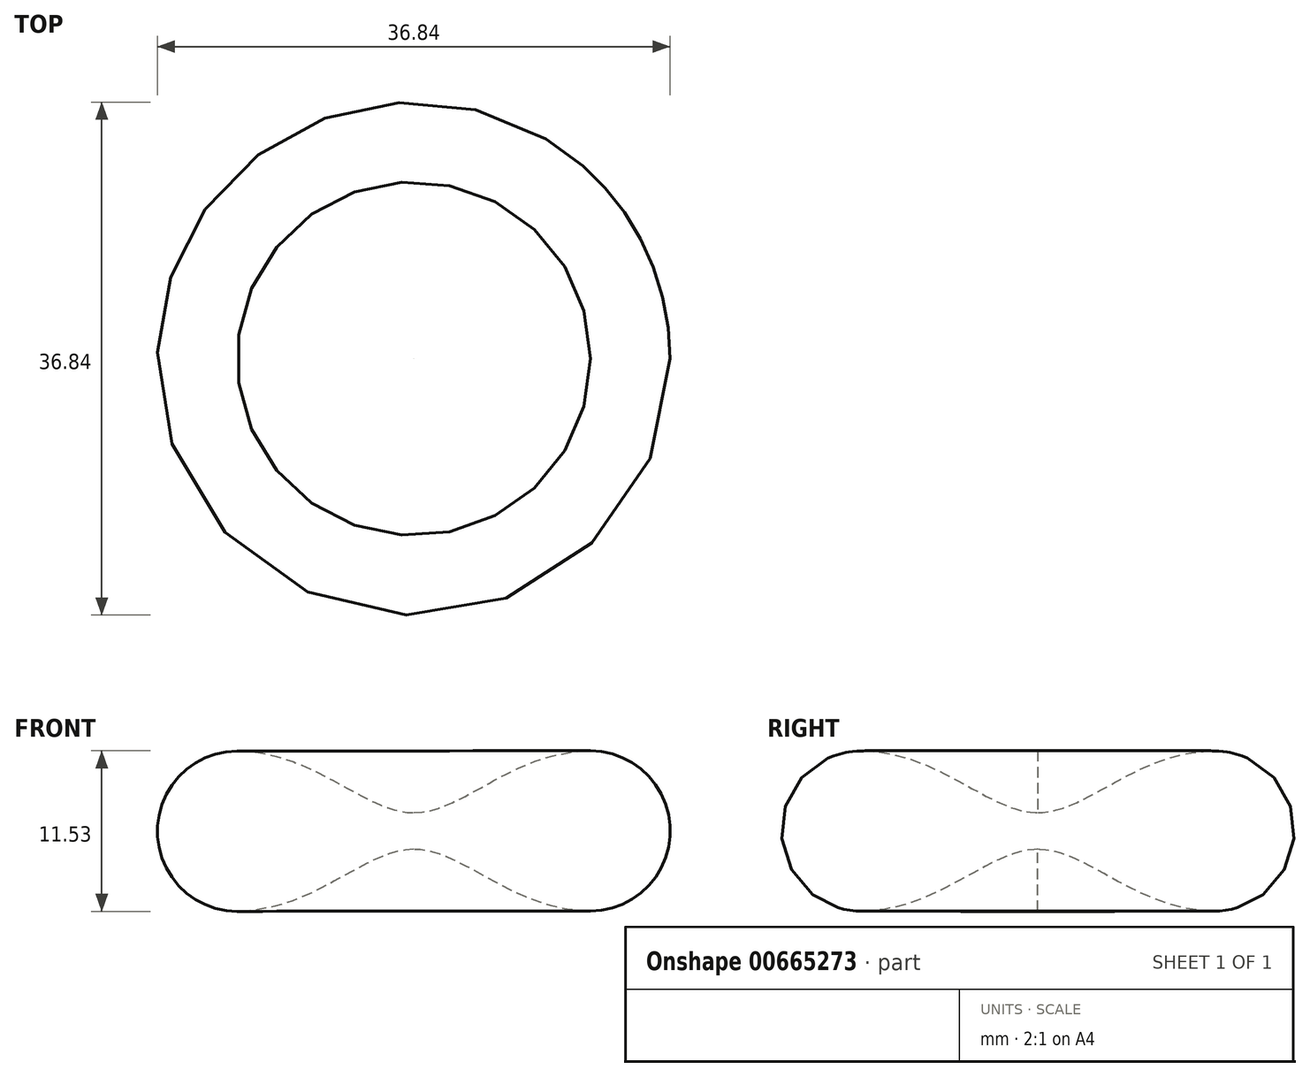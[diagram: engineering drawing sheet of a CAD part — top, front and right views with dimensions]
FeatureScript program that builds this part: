
annotation { "Feature Type Name" : "Feature", "Feature Type Description" : "" }
export const myFeature = defineFeature(function(context is Context, id is Id, definition is map)
    precondition{}
    {
        {
            var Q0;
            Q0=qCreatedBy(makeId("Front.planeOp"),FACE);
            var sketch = newSketch(context, id + "F0", { "sketchPlane" : qUnion([Q0])});
            skCircle(sketch, "E0", {"center": v(-12.67, 1.31) * mm, "radius": 5.76 * mm});
            skPoint(sketch, "E0.third.point", {"position": v(-18.3, 0.15) * mm});
            skCircle(sketch, "E1.MirrorC", {"center": v(12.73, 1.33) * mm, "radius": 5.77 * mm});
            skLineSegment(sketch, "E2", {"start": v(-12.67, 1.31) * mm, "end": v(12.73, 1.33) * mm});
            skLineSegment(sketch, "E3.0", {"start": v(-12.7, 0) * mm, "end": v(12.7, 0) * mm});
            skFitSpline(sketch, "E4", {"points": [v(-12.7, -4.45) * mm, v(0, 0) * mm, v(12.7, -4.45) * mm], "startDerivative": vector(33.28, 0) * mm, "endDerivative": vector(33.2, 0) * mm});
            skFitSpline(sketch, "E5.MirrorCS", {"points": [v(-12.7, 7.07) * mm, v(0, 2.64) * mm, v(12.7, 7.1) * mm], "startDerivative": vector(33.28, 0.04) * mm, "endDerivative": vector(33.2, 0.04) * mm});
            skLineSegment(sketch, "E6", {"start": v(0, 2.64) * mm, "end": v(0, 0) * mm});
            skSolve(sketch);
        }
        {
            var Q0;
            {var subQ0=sQuery(id+"F0.wireOp",EDGE,"E0");var subQ4=makeQuery(id+"F0.imprint","INTERSECT",VERTEX,{"derivedFrom":[subQ0,sQuery(id+"F0.wireOp",EDGE,"cc88ac5b-7040-4dbb-a68c-1f03ad9ae75d.0")]});Q0=makeQuery(id+"F0.imprint","IMPRINT",FACE,{"disambiguationData":[TD([[makeQuery(id+"F0.imprint","IMPRINT",EDGE,{"disambiguationData":[TD([[subQ4,1.0]])],"derivedFrom":subQ0}),1.0]])]});}
            var Q1;
            {var subQ0=sQuery(id+"F0.wireOp",EDGE,"E5.MirrorCS");var subQ1=sQuery(id+"F0.wireOp",EDGE,"E0");var subQ2=makeQuery(id+"F0.imprint","INTERSECT",VERTEX,{"derivedFrom":[subQ1,subQ0]});Q1=makeQuery(id+"F0.imprint","IMPRINT",FACE,{"disambiguationData":[TD([[makeQuery(id+"F0.imprint","IMPRINT",EDGE,{"disambiguationData":[TD([[subQ2,1.0]])],"derivedFrom":subQ1}),-1.0]])]});}
            var Q2;
            {var subQ1=sQuery(id+"F0.wireOp",EDGE,"cc88ac5b-7040-4dbb-a68c-1f03ad9ae75d.0");var subQ3=sQuery(id+"F0.wireOp",EDGE,"E0");var subQ4=makeQuery(id+"F0.imprint","INTERSECT",VERTEX,{"derivedFrom":[subQ3,subQ1]});Q2=makeQuery(id+"F0.imprint","IMPRINT",FACE,{"disambiguationData":[TD([[makeQuery(id+"F0.imprint","IMPRINT",EDGE,{"disambiguationData":[TD([[subQ4,1.0]])],"derivedFrom":subQ3}),-1.0]])]});}
            var Q3;
            {var subQ5=sQuery(id+"F0.wireOp",EDGE,"E0");var subQ7=sQuery(id+"F0.wireOp",EDGE,"E2");var subQ9=makeQuery(id+"F0.imprint","INTERSECT",VERTEX,{"derivedFrom":[subQ5,subQ7]});Q3=makeQuery(id+"F0.imprint","IMPRINT",FACE,{"disambiguationData":[TD([[makeQuery(id+"F0.imprint","IMPRINT",EDGE,{"disambiguationData":[TD([[subQ9,1.0]])],"derivedFrom":subQ5}),-1.0]])]});}
            var Q4;
            {var subQ0=sQuery(id+"F0.wireOp",EDGE,"E4");var subQ1=sQuery(id+"F0.wireOp",EDGE,"E0");var subQ2=makeQuery(id+"F0.imprint","INTERSECT",VERTEX,{"derivedFrom":[subQ1,subQ0]});Q4=makeQuery(id+"F0.imprint","IMPRINT",FACE,{"disambiguationData":[TD([[makeQuery(id+"F0.imprint","IMPRINT",EDGE,{"disambiguationData":[TD([[subQ2,-1.0]])],"derivedFrom":subQ1}),-1.0]])]});}
            var Q5;
            Q5=sQuery(id+"F0.wireOp",EDGE,"E6");
            revolve(context, id + "F1", {"entities" : qUnion([Q0, Q1, Q2, Q3, Q4]), "axis" : qUnion([Q5]), "revolveType" : RevolveType.FULL, "surfaceOperationType" : NewSurfaceOperationType.NEW});
        }
    });
